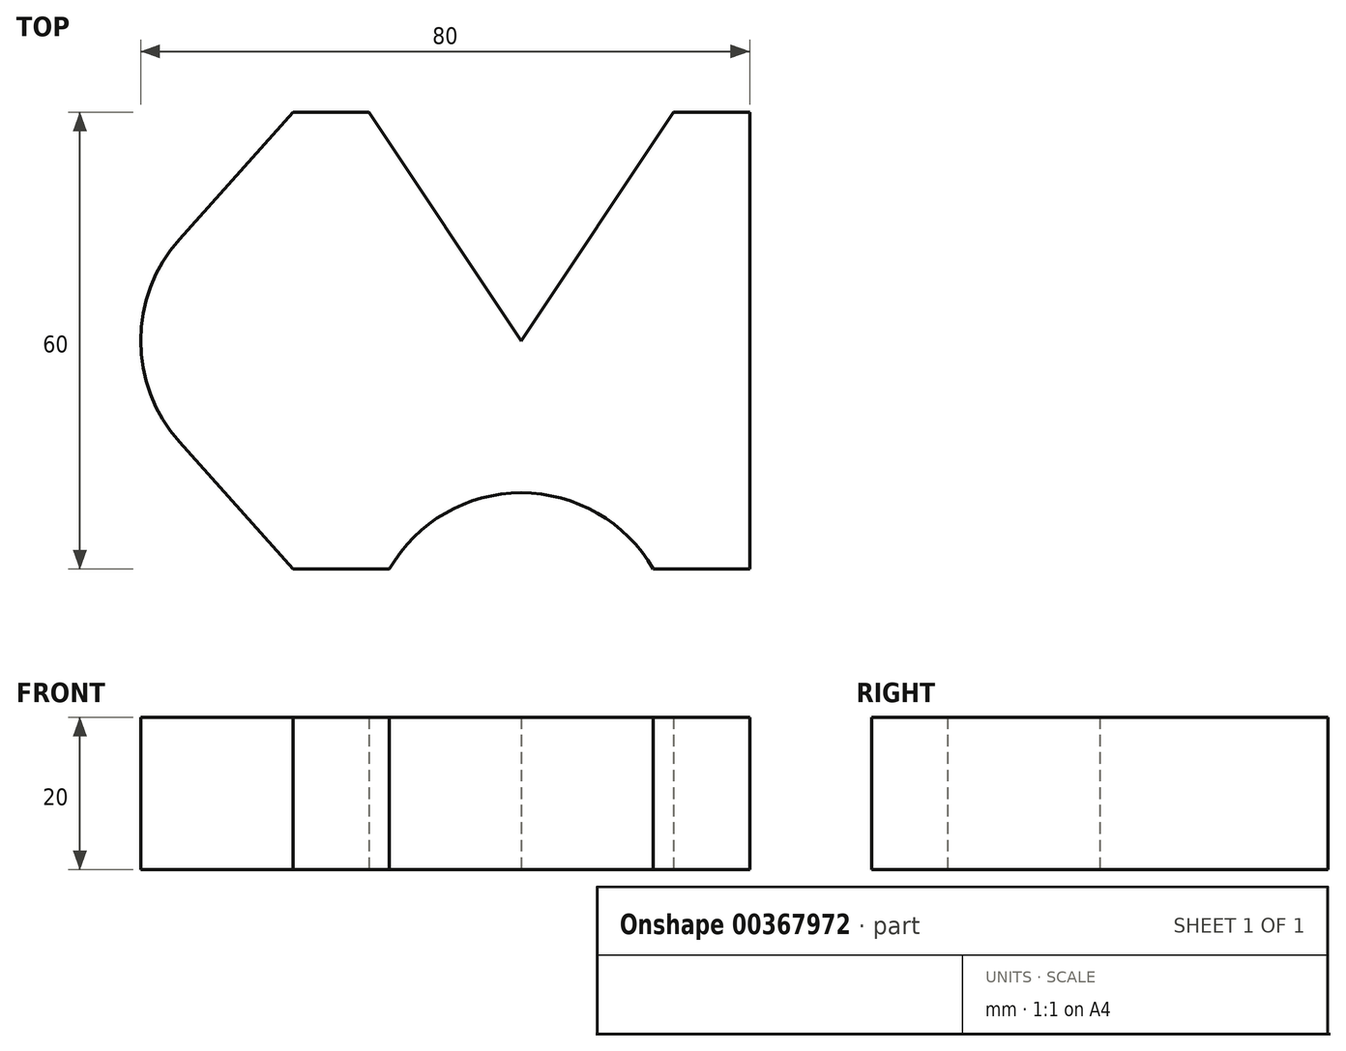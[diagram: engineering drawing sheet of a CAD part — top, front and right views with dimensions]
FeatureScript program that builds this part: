
annotation { "Feature Type Name" : "Feature", "Feature Type Description" : "" }
export const myFeature = defineFeature(function(context is Context, id is Id, definition is map)
    precondition{}
    {
        {
            var Q0;
            Q0=qCreatedBy(makeId("Top.planeOp"),FACE);
            var sketch = newSketch(context, id + "F0", { "sketchPlane" : qUnion([Q0])});
            skLineSegment(sketch, "E0", {"start": v(0, 0) * mm, "end": v(20, 30) * mm});
            skLineSegment(sketch, "E1", {"start": v(20, 30) * mm, "end": v(30, 30) * mm});
            skLineSegment(sketch, "E2", {"start": v(30, 30) * mm, "end": v(30, -30) * mm});
            skLineSegment(sketch, "E3", {"start": v(30, -30) * mm, "end": v(17.32, -30) * mm});
            skArc(sketch, "E4", {"start": v(17.32, -30) * mm, "mid": v(0, -20) * mm, "end": v(-17.32, -30) * mm});
            skLineSegment(sketch, "E5", {"start": v(-17.32, -30) * mm, "end": v(-30, -30) * mm});
            skLineSegment(sketch, "E6", {"start": v(-30, -30) * mm, "end": v(-44.9, -13.33) * mm});
            skArc(sketch, "E7", {"start": v(-44.9, 13.33) * mm, "mid": v(-50, 0) * mm, "end": v(-44.9, -13.33) * mm});
            skLineSegment(sketch, "E8", {"start": v(-44.9, 13.33) * mm, "end": v(-30, 30) * mm});
            skLineSegment(sketch, "E9", {"start": v(-30, 30) * mm, "end": v(-20, 30) * mm});
            skLineSegment(sketch, "E10", {"start": v(-20, 30) * mm, "end": v(0, 0) * mm});
            skLineSegment(sketch, "E11", {"start": v(-30, 30) * mm, "end": v(-30, -30) * mm, "construction": true});
            skSolve(sketch);
        }
        {
            var Q0;
            Q0=makeQuery(id+"F0.imprint","IMPRINT",FACE,{"disambiguationData":[TD([[makeQuery(id+"F0.imprint","IMPRINT",EDGE,{"derivedFrom":sQuery(id+"F0.wireOp",EDGE,"E0")}),-1.0]])]});
            extrude(context, id + "F1", {"entities" : qUnion([Q0]), "depth" : 20 * mm});
        }
    });
